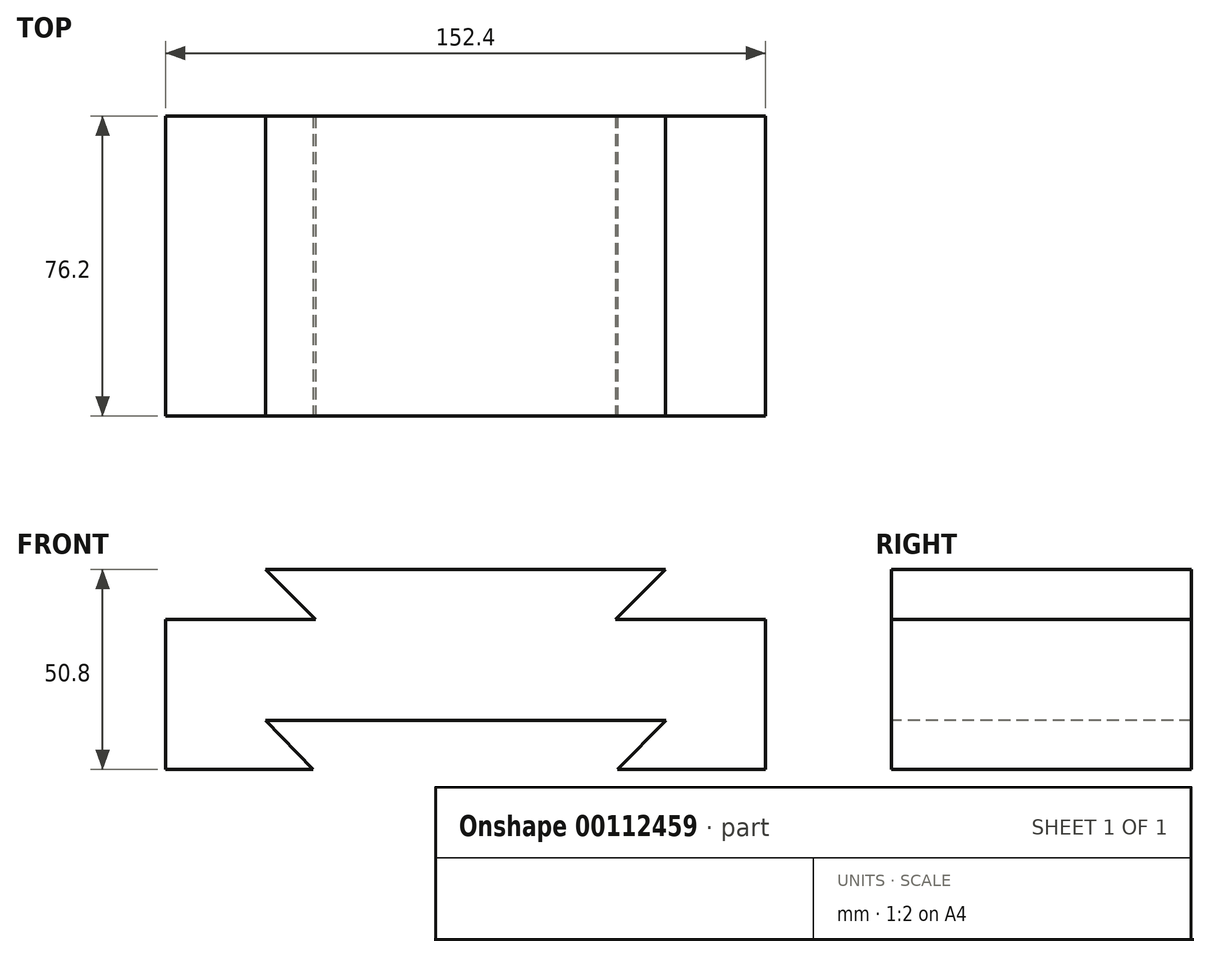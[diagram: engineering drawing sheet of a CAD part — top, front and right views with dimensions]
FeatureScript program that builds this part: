
annotation { "Feature Type Name" : "Feature", "Feature Type Description" : "" }
export const myFeature = defineFeature(function(context is Context, id is Id, definition is map)
    precondition{}
    {
        {
            var Q0;
            Q0=qCreatedBy(makeId("Top.planeOp"),FACE);
            var sketch = newSketch(context, id + "F0", { "sketchPlane" : qUnion([Q0])});
            skLineSegment(sketch, "E0.bottom", {"start": v(-76.2, 38.1) * mm, "end": v(76.2, 38.1) * mm});
            skLineSegment(sketch, "E0.top", {"start": v(-76.2, -38.1) * mm, "end": v(76.2, -38.1) * mm});
            skLineSegment(sketch, "E0.left", {"start": v(-76.2, 38.1) * mm, "end": v(-76.2, -38.1) * mm});
            skLineSegment(sketch, "E0.right", {"start": v(76.2, 38.1) * mm, "end": v(76.2, -38.1) * mm});
            skPoint(sketch, "E0.middle", {"position": v(0, 0) * mm});
            skSolve(sketch);
        }
        {
            var Q0;
            Q0 = qSketchRegion(id + "F0", true);
            extrude(context, id + "F1", {"entities" : qUnion([Q0]), "depth" : 50.8 * mm});
        }
        {
            var Q0;
            Q0=makeQuery(id+"F1.opExtrude","CAP_FACE",FACE,{"disambiguationData":[OSD([sQuery(id+"F0.wireOp",EDGE,"E0.bottom"),sQuery(id+"F0.wireOp",EDGE,"E0.top"),sQuery(id+"F0.wireOp",EDGE,"E0.left"),sQuery(id+"F0.wireOp",EDGE,"E0.right")])],"isStart":false});
            var sketch = newSketch(context, id + "F2", { "sketchPlane" : qUnion([Q0])});
            skLineSegment(sketch, "E1.bottom", {"start": v(76.2, 38.1) * mm, "end": v(50.8, 38.1) * mm});
            skLineSegment(sketch, "E1.top", {"start": v(76.2, -38.1) * mm, "end": v(50.8, -38.1) * mm});
            skLineSegment(sketch, "E1.left", {"start": v(76.2, 38.1) * mm, "end": v(76.2, -38.1) * mm});
            skLineSegment(sketch, "E1.right", {"start": v(50.8, 38.1) * mm, "end": v(50.8, -38.1) * mm});
            skSolve(sketch);
        }
        {
            var Q0;
            Q0 = qSketchRegion(id + "F2", true);
            extrude(context, id + "F3", {"entities" : qUnion([Q0]), "operationType" : NewBodyOperationType.REMOVE, "oppositeDirection" : true, "depth" : 12.7 * mm});
        }
        {
            var Q0;
            Q0=makeQuery(id+"F1.opExtrude","CAP_FACE",FACE,{"disambiguationData":[OSD([sQuery(id+"F0.wireOp",EDGE,"E0.bottom"),sQuery(id+"F0.wireOp",EDGE,"E0.top"),sQuery(id+"F0.wireOp",EDGE,"E0.left"),sQuery(id+"F0.wireOp",EDGE,"E0.right")])],"isStart":false});
            var sketch = newSketch(context, id + "F4", { "sketchPlane" : qUnion([Q0])});
            skLineSegment(sketch, "E2.bottom", {"start": v(-76.2, 38.1) * mm, "end": v(-50.8, 38.1) * mm});
            skLineSegment(sketch, "E2.top", {"start": v(-76.2, -38.1) * mm, "end": v(-50.8, -38.1) * mm});
            skLineSegment(sketch, "E2.left", {"start": v(-76.2, 38.1) * mm, "end": v(-76.2, -38.1) * mm});
            skLineSegment(sketch, "E2.right", {"start": v(-50.8, 38.1) * mm, "end": v(-50.8, -38.1) * mm});
            skSolve(sketch);
        }
        {
            var Q0;
            Q0 = qSketchRegion(id + "F4", true);
            extrude(context, id + "F5", {"entities" : qUnion([Q0]), "operationType" : NewBodyOperationType.REMOVE, "oppositeDirection" : true, "depth" : 12.7 * mm});
        }
        {
            var Q0;
            Q0=makeQuery(id+"F1.opExtrude","SWEPT_FACE",FACE,{"disambiguationData":[OSD([sQuery(id+"F0.wireOp",EDGE,"E0.top")])]});
            var sketch = newSketch(context, id + "F6", { "sketchPlane" : qUnion([Q0])});
            skLineSegment(sketch, "E3", {"start": v(-50.8, 38.1) * mm, "end": v(-50.8, 50.8) * mm});
            skLineSegment(sketch, "E4", {"start": v(-50.8, 38.1) * mm, "end": v(-38.1, 38.1) * mm});
            skLineSegment(sketch, "E5", {"start": v(-50.8, 50.8) * mm, "end": v(-38.1, 38.1) * mm});
            skSolve(sketch);
        }
        {
            var Q0;
            Q0 = qSketchRegion(id + "F6", true);
            extrude(context, id + "F7", {"entities" : qUnion([Q0]), "operationType" : NewBodyOperationType.REMOVE, "endBound" : BoundingType.THROUGH_ALL, "oppositeDirection" : true, "depth" : 25.4 * mm});
        }
        {
            var Q0;
            Q0=makeQuery(id+"F1.opExtrude","SWEPT_FACE",FACE,{"disambiguationData":[OSD([sQuery(id+"F0.wireOp",EDGE,"E0.top")])]});
            var sketch = newSketch(context, id + "F8", { "sketchPlane" : qUnion([Q0])});
            skLineSegment(sketch, "E6", {"start": v(50.8, 38.1) * mm, "end": v(50.8, 50.8) * mm});
            skLineSegment(sketch, "E7", {"start": v(50.8, 38.1) * mm, "end": v(38.1, 38.1) * mm});
            skLineSegment(sketch, "E8", {"start": v(38.1, 38.1) * mm, "end": v(50.8, 50.8) * mm});
            skSolve(sketch);
        }
        {
            var Q0;
            Q0 = qSketchRegion(id + "F8", true);
            extrude(context, id + "F9", {"entities" : qUnion([Q0]), "operationType" : NewBodyOperationType.REMOVE, "endBound" : BoundingType.THROUGH_ALL, "oppositeDirection" : true, "depth" : 25.4 * mm});
        }
        {
            var Q0;
            Q0=makeQuery(id+"F1.opExtrude","SWEPT_FACE",FACE,{"disambiguationData":[OSD([sQuery(id+"F0.wireOp",EDGE,"E0.top")])]});
            var sketch = newSketch(context, id + "F10", { "sketchPlane" : qUnion([Q0])});
            skLineSegment(sketch, "E9", {"start": v(76.2, 0) * mm, "end": v(38.1, 0) * mm});
            skLineSegment(sketch, "E10", {"start": v(-76.2, 0) * mm, "end": v(-38.1, 0) * mm});
            skLineSegment(sketch, "E11", {"start": v(-76.2, 0) * mm, "end": v(-50.8, 0) * mm});
            skLineSegment(sketch, "E12", {"start": v(76.2, 0) * mm, "end": v(50.8, 0) * mm});
            skLineSegment(sketch, "E13", {"start": v(50.8, 0) * mm, "end": v(50.8, 7.34) * mm});
            skLineSegment(sketch, "E14", {"start": v(-50.8, 0) * mm, "end": v(-50.8, 12.7) * mm});
            skLineSegment(sketch, "E15", {"start": v(50.8, 0) * mm, "end": v(50.8, 12.7) * mm});
            skSolve(sketch);
        }
        {
            var Q0;
            {var subQ1=sQuery(id+"F10.wireOp",EDGE,"E9");Q0=makeQuery(id+"F10.imprint","IMPRINT",FACE,{"disambiguationData":[TD([[makeQuery(id+"F10.imprint","IMPRINT",EDGE,{"derivedFrom":subQ1}),1.0]])]});}
            var sketch = newSketch(context, id + "F11", { "sketchPlane" : qUnion([Q0])});
            skLineSegment(sketch, "E16", {"start": v(-38.73, 0) * mm, "end": v(-50.8, 12.52) * mm});
            skLineSegment(sketch, "E17", {"start": v(-50.8, 12.52) * mm, "end": v(50.94, 12.52) * mm});
            skLineSegment(sketch, "E18", {"start": v(50.94, 12.52) * mm, "end": v(38.62, 0) * mm});
            skLineSegment(sketch, "E19", {"start": v(38.62, 0) * mm, "end": v(-38.73, 0) * mm});
            skSolve(sketch);
        }
        {
            var Q0;
            Q0 = qSketchRegion(id + "F11", true);
            extrude(context, id + "F12", {"entities" : qUnion([Q0]), "operationType" : NewBodyOperationType.REMOVE, "endBound" : BoundingType.THROUGH_ALL, "oppositeDirection" : true, "depth" : 25.4 * mm});
        }
    });
